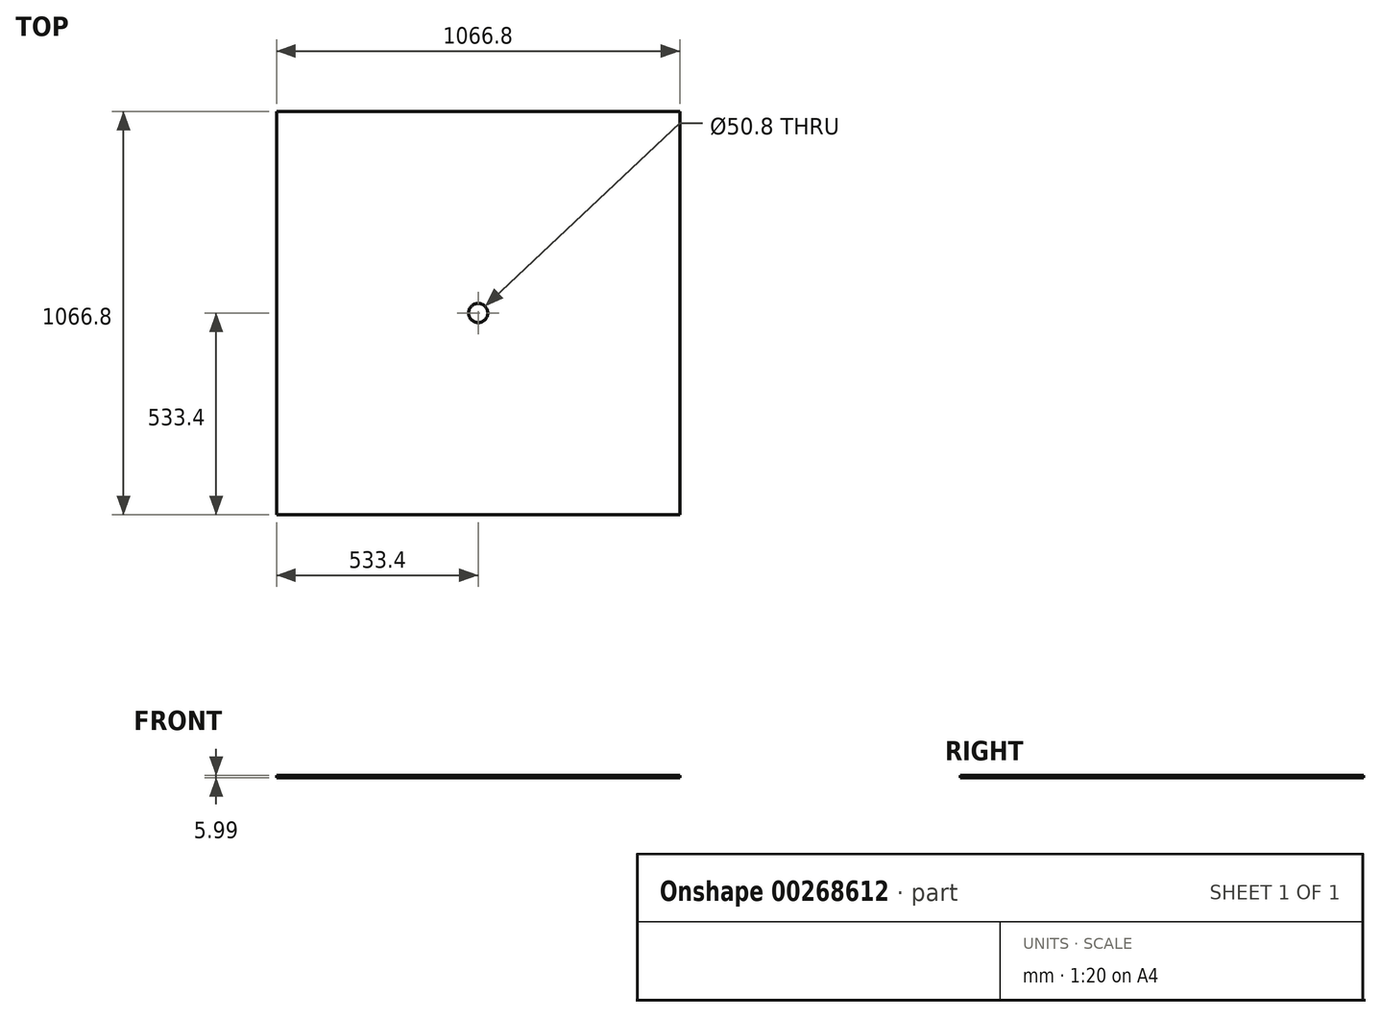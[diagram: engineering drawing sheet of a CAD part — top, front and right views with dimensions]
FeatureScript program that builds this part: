
annotation { "Feature Type Name" : "Feature", "Feature Type Description" : "" }
export const myFeature = defineFeature(function(context is Context, id is Id, definition is map)
    precondition{}
    {
        {
            var Q0;
            Q0=qCreatedBy(makeId("Top.planeOp"),FACE);
            var sketch = newSketch(context, id + "F0", { "sketchPlane" : qUnion([Q0])});
            skLineSegment(sketch, "E0.bottom", {"start": v(533.4, -533.4) * mm, "end": v(-533.4, -533.4) * mm});
            skLineSegment(sketch, "E0.top", {"start": v(533.4, 533.4) * mm, "end": v(-533.4, 533.4) * mm});
            skLineSegment(sketch, "E0.left", {"start": v(533.4, -533.4) * mm, "end": v(533.4, 533.4) * mm});
            skLineSegment(sketch, "E0.right", {"start": v(-533.4, -533.4) * mm, "end": v(-533.4, 533.4) * mm});
            skPoint(sketch, "E0.middle", {"position": v(0, 0) * mm});
            skCircle(sketch, "E1", {"center": v(0, 0) * mm, "radius": 25.4 * mm});
            skSolve(sketch);
        }
        {
            var Q0;
            Q0=makeQuery(id+"F0.imprint","IMPRINT",FACE,{"disambiguationData":[TD([[makeQuery(id+"F0.imprint","IMPRINT",EDGE,{"derivedFrom":sQuery(id+"F0.wireOp",EDGE,"E0.bottom")}),-1.0]])]});
            extrude(context, id + "F1", {"entities" : qUnion([Q0]), "depth" : 6 * mm});
        }
    });
